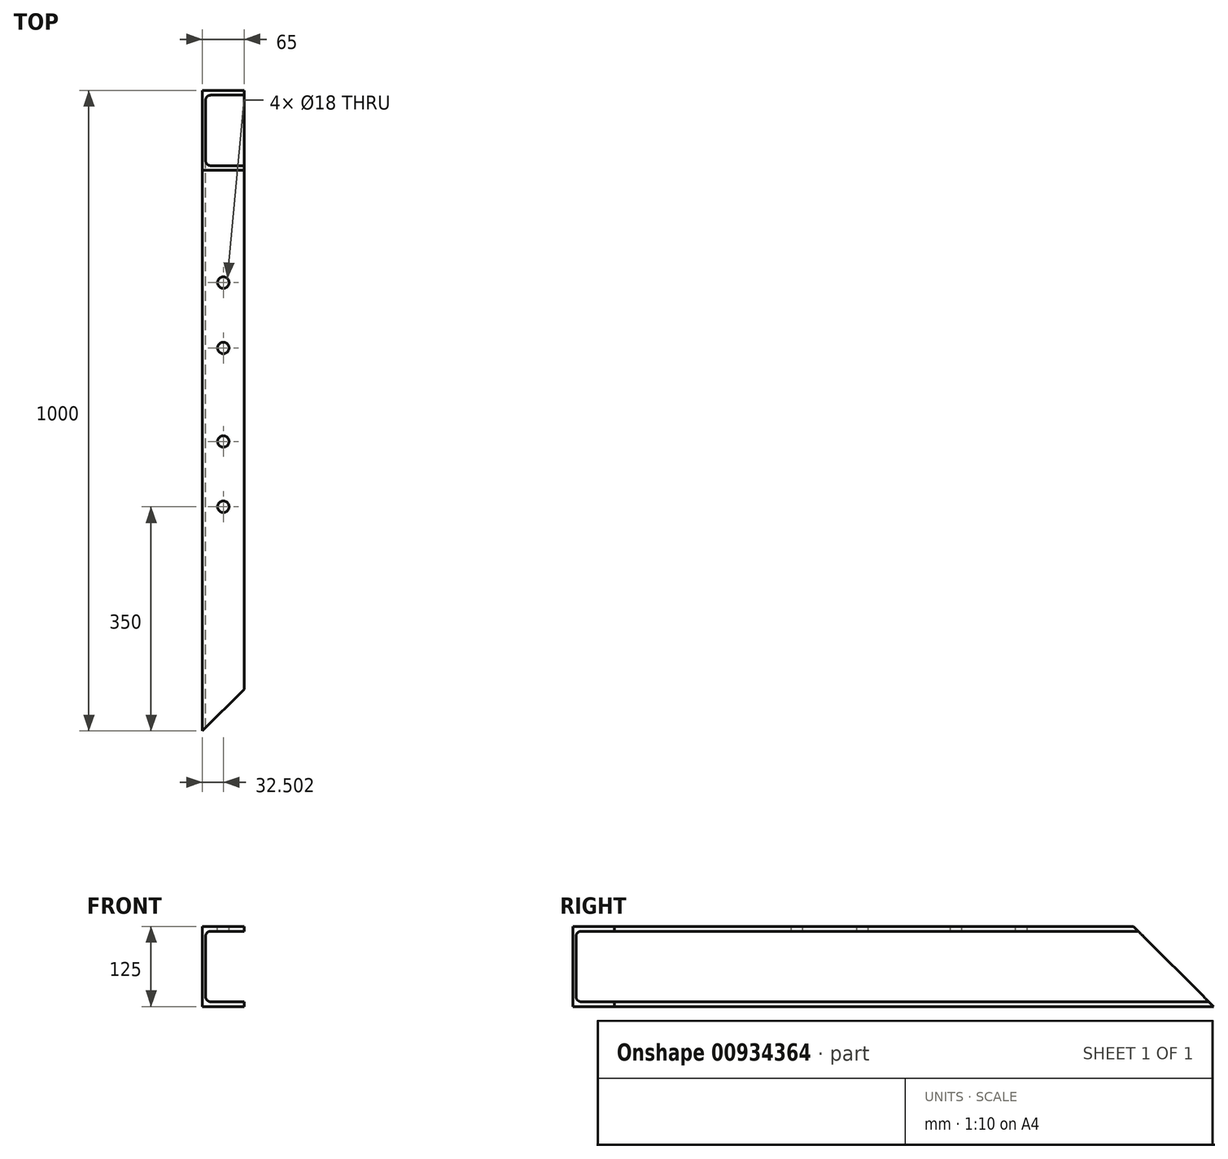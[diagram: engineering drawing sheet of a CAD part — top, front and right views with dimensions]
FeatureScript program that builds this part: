
annotation { "Feature Type Name" : "Feature", "Feature Type Description" : "" }
export const myFeature = defineFeature(function(context is Context, id is Id, definition is map)
    precondition{}
    {
        {
            var Q0;
            Q0=qCreatedBy(makeId("Front.planeOp"),FACE);
            var sketch = newSketch(context, id + "F0", { "sketchPlane" : qUnion([Q0])});
            skLineSegment(sketch, "E0", {"start": v(-25.17, -62.5) * mm, "end": v(-25.17, 62.5) * mm});
            skLineSegment(sketch, "E1", {"start": v(-25.17, 62.5) * mm, "end": v(39.83, 62.5) * mm});
            skLineSegment(sketch, "E2", {"start": v(39.83, 62.5) * mm, "end": v(39.83, 55) * mm});
            skLineSegment(sketch, "E3", {"start": v(39.83, 55) * mm, "end": v(-12.47, 55) * mm});
            skLineSegment(sketch, "E4", {"start": v(-25.17, -62.5) * mm, "end": v(39.83, -62.5) * mm});
            skLineSegment(sketch, "E5", {"start": v(39.83, -62.5) * mm, "end": v(39.83, -55) * mm});
            skLineSegment(sketch, "E6", {"start": v(39.83, -55) * mm, "end": v(-12.47, -55) * mm});
            skLineSegment(sketch, "E7", {"start": v(-20.47, -47) * mm, "end": v(-20.47, 47) * mm});
            skPoint(sketch, "E8.visualSharp", {"position": v(-20.47, 55) * mm});
            skArc(sketch, "E8.filletArc", {"start": v(-12.47, 55) * mm, "mid": v(-18.12, 52.66) * mm, "end": v(-20.47, 47) * mm});
            skPoint(sketch, "E9.visualSharp", {"position": v(-20.47, -55) * mm});
            skArc(sketch, "E9.filletArc", {"start": v(-20.47, -47) * mm, "mid": v(-18.12, -52.66) * mm, "end": v(-12.47, -55) * mm});
            skSolve(sketch);
        }
        {
            var Q0;
            Q0=makeQuery(id+"F0.imprint","IMPRINT",FACE,{"disambiguationData":[TD([[makeQuery(id+"F0.imprint","IMPRINT",EDGE,{"derivedFrom":sQuery(id+"F0.wireOp",EDGE,"E0")}),-1.0]])]});
            extrude(context, id + "F1", {"entities" : qUnion([Q0]), "depth" : 1000 * mm, "offsetDistance" : 25 * mm});
        }
        {
            var Q0;
            Q0=makeQuery(id+"F1.opExtrude","SWEPT_FACE",FACE,{"disambiguationData":[OSD([sQuery(id+"F0.wireOp",EDGE,"E0")])]});
            var sketch = newSketch(context, id + "F2", { "sketchPlane" : qUnion([Q0])});
            skLineSegment(sketch, "E10", {"start": v(0, 62.5) * mm, "end": v(125, 62.5) * mm});
            skLineSegment(sketch, "E11", {"start": v(125, 62.5) * mm, "end": v(0, -62.5) * mm});
            skSolve(sketch);
        }
        {
            var Q0;
            Q0=makeQuery(id+"F2.imprint","IMPRINT",FACE,{"disambiguationData":[TD([[makeQuery(id+"F2.imprint","IMPRINT",EDGE,{"derivedFrom":sQuery(id+"F2.wireOp",EDGE,"E10")}),1.0]])]});
            extrude(context, id + "F3", {"entities" : qUnion([Q0]), "operationType" : NewBodyOperationType.REMOVE, "endBound" : BoundingType.THROUGH_ALL, "oppositeDirection" : true, "depth" : 25 * mm, "offsetDistance" : 25 * mm});
        }
        {
            var Q0;
            Q0=makeQuery(id+"F1.opExtrude","SWEPT_FACE",FACE,{"disambiguationData":[OSD([sQuery(id+"F0.wireOp",EDGE,"E1")])]});
            var sketch = newSketch(context, id + "F4", { "sketchPlane" : qUnion([Q0])});
            skLineSegment(sketch, "E12", {"start": v(39.83, -1000) * mm, "end": v(39.83, -935) * mm});
            skLineSegment(sketch, "E13", {"start": v(39.83, -935) * mm, "end": v(-25.17, -1000) * mm});
            skSolve(sketch);
        }
        {
            var Q0;
            Q0=makeQuery(id+"F4.imprint","IMPRINT",FACE,{"disambiguationData":[TD([[makeQuery(id+"F4.imprint","IMPRINT",EDGE,{"derivedFrom":sQuery(id+"F4.wireOp",EDGE,"E12")}),1.0]])]});
            extrude(context, id + "F5", {"entities" : qUnion([Q0]), "operationType" : NewBodyOperationType.REMOVE, "endBound" : BoundingType.THROUGH_ALL, "oppositeDirection" : true, "depth" : 25 * mm, "offsetDistance" : 25 * mm});
        }
        {
            var Q0;
            Q0=makeQuery(id+"F1.opExtrude","SWEPT_FACE",FACE,{"disambiguationData":[OSD([sQuery(id+"F0.wireOp",EDGE,"E1")])]});
            var sketch = newSketch(context, id + "F6", { "sketchPlane" : qUnion([Q0])});
            skLineSegment(sketch, "E14", {"start": v(-25.17, -1000) * mm, "end": v(-25.17, -650) * mm, "construction": true});
            skLineSegment(sketch, "E15", {"start": v(-25.17, -650) * mm, "end": v(7.33, -650) * mm, "construction": true});
            skLineSegment(sketch, "E16", {"start": v(7.33, -650) * mm, "end": v(7.33, -548) * mm, "construction": true});
            skCircle(sketch, "E17", {"center": v(7.33, -548) * mm, "radius": 9 * mm});
            skCircle(sketch, "E18", {"center": v(7.33, -650) * mm, "radius": 9 * mm});
            skSolve(sketch);
        }
        {
            var Q0;
            Q0 = qSketchRegion(id + "F6", true);
            extrude(context, id + "F7", {"entities" : qUnion([Q0]), "operationType" : NewBodyOperationType.REMOVE, "endBound" : BoundingType.UP_TO_NEXT, "oppositeDirection" : true, "depth" : 25 * mm, "offsetDistance" : 25 * mm});
        }
        {
            var Q0;
            Q0=makeQuery(id+"F1.opExtrude","SWEPT_FACE",FACE,{"disambiguationData":[OSD([sQuery(id+"F0.wireOp",EDGE,"E1")])]});
            var sketch = newSketch(context, id + "F8", { "sketchPlane" : qUnion([Q0])});
            skCircle(sketch, "E19", {"center": v(7.33, -300) * mm, "radius": 9 * mm});
            skCircle(sketch, "E20", {"center": v(7.33, -402) * mm, "radius": 9 * mm});
            skLineSegment(sketch, "E21", {"start": v(7.33, -300) * mm, "end": v(7.33, -402) * mm, "construction": true});
            skLineSegment(sketch, "E22", {"start": v(7.33, -300) * mm, "end": v(7.33, -125) * mm, "construction": true});
            skSolve(sketch);
        }
        {
            var Q0;
            Q0 = qSketchRegion(id + "F8", true);
            extrude(context, id + "F9", {"entities" : qUnion([Q0]), "operationType" : NewBodyOperationType.REMOVE, "endBound" : BoundingType.UP_TO_NEXT, "oppositeDirection" : true, "depth" : 25 * mm, "offsetDistance" : 25 * mm});
        }
    });
